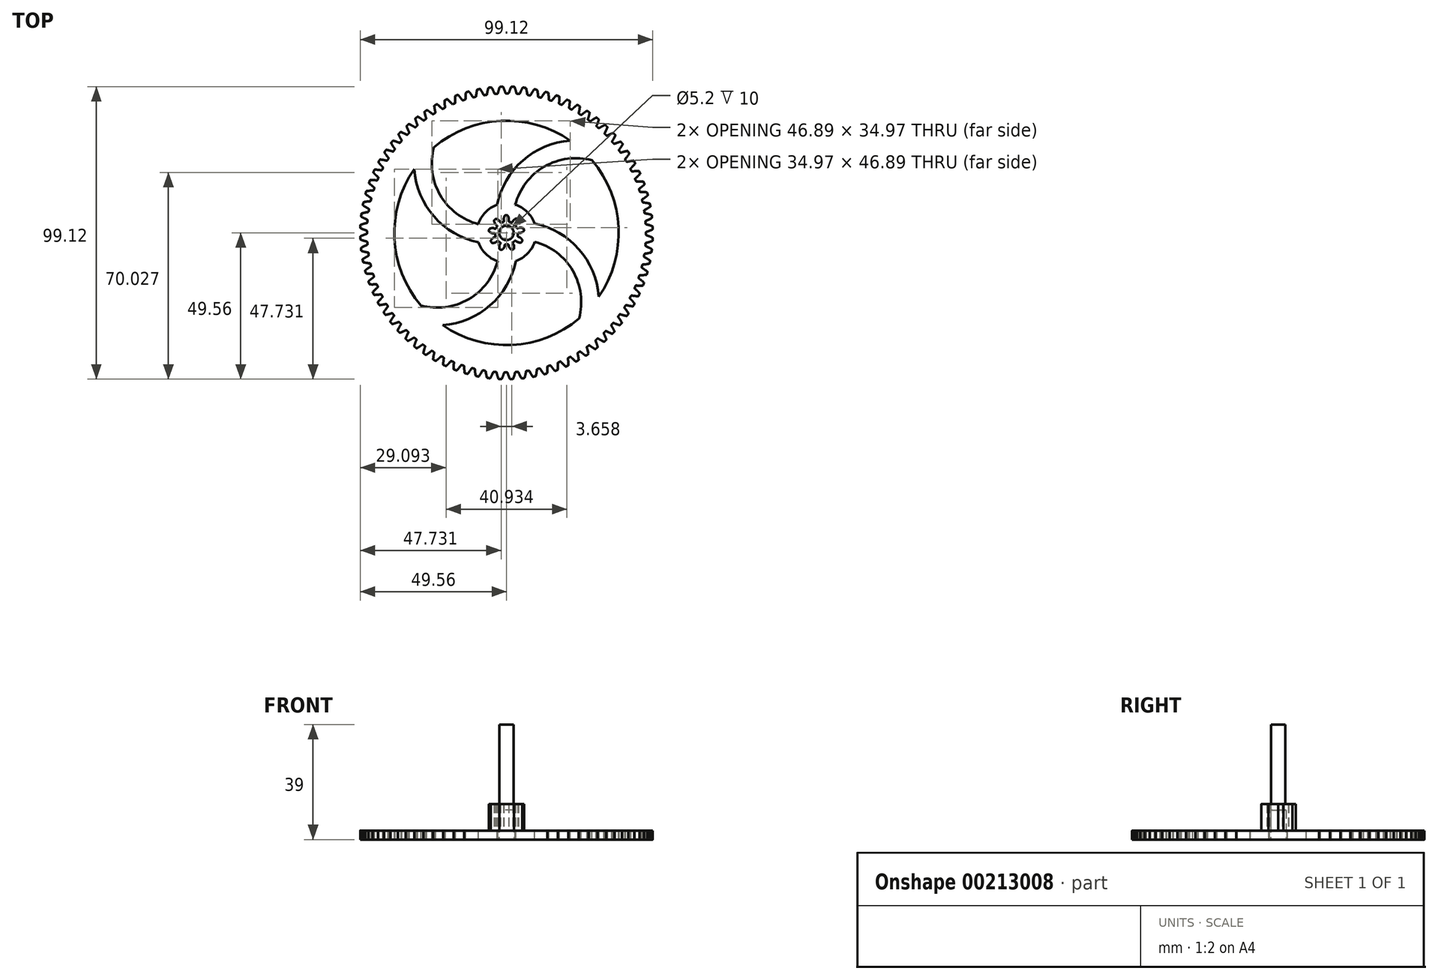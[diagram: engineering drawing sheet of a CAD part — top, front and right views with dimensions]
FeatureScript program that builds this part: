
annotation { "Feature Type Name" : "Feature", "Feature Type Description" : "" }
export const myFeature = defineFeature(function(context is Context, id is Id, definition is map)
    precondition{}
    {
        {
            var Q0;
            Q0=qCreatedBy(makeId("Top.planeOp"),FACE);
            var sketch = newSketch(context, id + "F0", { "sketchPlane" : qUnion([Q0])});
            skCircle(sketch, "E0", {"center": v(0, 0) * mm, "radius": 45.56 * mm, "construction": true});
            skLineSegment(sketch, "E1", {"start": v(0, 0) * mm, "end": v(45.56, 0) * mm, "construction": true});
            skLineSegment(sketch, "E2", {"start": v(45.56, 0) * mm, "end": v(45.56, 0) * mm});
            skLineSegment(sketch, "E3", {"start": v(0, 0) * mm, "end": v(45.52, 1.99) * mm, "construction": true});
            skLineSegment(sketch, "E4", {"start": v(45.52, 1.99) * mm, "end": v(45.6, 0) * mm, "construction": true});
            skLineSegment(sketch, "E5", {"start": v(0, 0) * mm, "end": v(45.39, 3.97) * mm, "construction": true});
            skLineSegment(sketch, "E6", {"start": v(45.39, 3.97) * mm, "end": v(45.73, 0.01) * mm, "construction": true});
            skLineSegment(sketch, "E7", {"start": v(0, 0) * mm, "end": v(45.17, 5.95) * mm, "construction": true});
            skLineSegment(sketch, "E8", {"start": v(45.17, 5.95) * mm, "end": v(45.95, 0.03) * mm, "construction": true});
            skLineSegment(sketch, "E9", {"start": v(0, 0) * mm, "end": v(44.87, 7.91) * mm, "construction": true});
            skLineSegment(sketch, "E10", {"start": v(44.87, 7.91) * mm, "end": v(46.25, 0.08) * mm, "construction": true});
            skLineSegment(sketch, "E11", {"start": v(0, 0) * mm, "end": v(44.48, 9.86) * mm, "construction": true});
            skLineSegment(sketch, "E12", {"start": v(44.48, 9.86) * mm, "end": v(46.63, 0.16) * mm, "construction": true});
            skLineSegment(sketch, "E13", {"start": v(0, 0) * mm, "end": v(44, 11.8) * mm, "construction": true});
            skLineSegment(sketch, "E14", {"start": v(44, 11.8) * mm, "end": v(47.1, 0.27) * mm, "construction": true});
            skLineSegment(sketch, "E15", {"start": v(0, 0) * mm, "end": v(43.45, 13.7) * mm, "construction": true});
            skLineSegment(sketch, "E16", {"start": v(43.45, 13.7) * mm, "end": v(47.64, 0.43) * mm, "construction": true});
            skLineSegment(sketch, "E17", {"start": v(0, 0) * mm, "end": v(42.81, 15.58) * mm, "construction": true});
            skLineSegment(sketch, "E18", {"start": v(42.81, 15.58) * mm, "end": v(48.25, 0.64) * mm, "construction": true});
            skLineSegment(sketch, "E19", {"start": v(0, 0) * mm, "end": v(42.1, 17.44) * mm, "construction": true});
            skLineSegment(sketch, "E20", {"start": v(42.1, 17.44) * mm, "end": v(48.94, 0.9) * mm, "construction": true});
            skLineSegment(sketch, "E21", {"start": v(0, 0) * mm, "end": v(41.3, 19.25) * mm, "construction": true});
            skLineSegment(sketch, "E22", {"start": v(41.3, 19.25) * mm, "end": v(49.7, 1.24) * mm, "construction": true});
            skPoint(sketch, "E23", {"position": v(45.56, 0) * mm});
            skLineSegment(sketch, "E24", {"start": v(0, 0) * mm, "end": v(55.62, 1.92) * mm, "construction": true});
            skFitSpline(sketch, "E25", {"points": [v(45.45, 3.14) * mm, v(45.5, 3.15) * mm, v(45.63, 3.15) * mm, v(45.84, 3.14) * mm, v(46.14, 3.11) * mm, v(46.53, 3.06) * mm, v(47, 2.98) * mm, v(47.55, 2.86) * mm, v(48.18, 2.7) * mm, v(48.89, 2.47) * mm, v(49.66, 2.2) * mm], "startDerivative": vector(1.04, 0.05) * mm, "endDerivative": vector(4.91, -1.82) * mm});
            skFitSpline(sketch, "E26", {"points": [v(45.56, 0) * mm, v(45.6, 0) * mm, v(45.73, 0.01) * mm, v(45.95, 0.03) * mm, v(46.25, 0.08) * mm, v(46.63, 0.16) * mm, v(47.1, 0.27) * mm, v(47.64, 0.43) * mm, v(48.25, 0.64) * mm, v(48.94, 0.9) * mm, v(49.7, 1.24) * mm], "startDerivative": vector(1.04, 0.02) * mm, "endDerivative": vector(4.78, 2.16) * mm});
            skArc(sketch, "E27", {"start": v(49.52, 2.25) * mm, "mid": v(-49.55, -1.71) * mm, "end": v(49.56, 1.18) * mm, "construction": true});
            skArc(sketch, "E28", {"start": v(49.56, 1.18) * mm, "mid": v(49.55, 1.71) * mm, "end": v(49.52, 2.25) * mm});
            skArc(sketch, "E29", {"start": v(47.18, 2.94) * mm, "mid": v(-47.24, -1.63) * mm, "end": v(47.27, 0.32) * mm});
            skArc(sketch, "E30", {"start": v(47.27, 0.32) * mm, "mid": v(47.24, 1.63) * mm, "end": v(47.18, 2.94) * mm, "construction": true});
            skSolve(sketch);
        }
        {
            var Q0;
            Q0=qCreatedBy(makeId("Front.planeOp"),FACE);
            var sketch = newSketch(context, id + "F1", { "sketchPlane" : qUnion([Q0])});
            skLineSegment(sketch, "E31", {"start": v(0, 0) * mm, "end": v(0, 19.36) * mm});
            skSolve(sketch);
        }
        {
            var Q0;
            {var subQ0=sQuery(id+"F0.wireOp",EDGE,"E28");Q0=makeQuery(id+"F0.imprint","IMPRINT",FACE,{"disambiguationData":[TD([[makeQuery(id+"F0.imprint","IMPRINT",EDGE,{"derivedFrom":subQ0}),1.0]])]});}
            extrude(context, id + "F2", {"entities" : qUnion([Q0]), "depth" : 3 * mm});
        }
        {
            var Q0;
            Q0=makeQuery(id+"F2.opExtrude","SWEPT_EDGE",EDGE,{"disambiguationData":[OSD([sQuery(id+"F0.wireOp",EDGE,"E25"),sQuery(id+"F0.wireOp",EDGE,"cd1f8e22-2cf9-43e8-a03b-3c7e5e83a7e11")])]});
            var Q1;
            Q1=makeQuery(id+"F2.opExtrude","SWEPT_EDGE",EDGE,{"disambiguationData":[OSD([sQuery(id+"F0.wireOp",EDGE,"E25"),sQuery(id+"F0.wireOp",EDGE,"6e4f36b8-18ed-47d9-b409-67013e73f9462")])]});
            var Q2;
            Q2=makeQuery(id+"F2.opExtrude","SWEPT_EDGE",EDGE,{"disambiguationData":[OSD([sQuery(id+"F0.wireOp",EDGE,"E26"),sQuery(id+"F0.wireOp",EDGE,"6e4f36b8-18ed-47d9-b409-67013e73f9462")])]});
            var Q3;
            Q3=makeQuery(id+"F2.opExtrude","SWEPT_EDGE",EDGE,{"disambiguationData":[OSD([sQuery(id+"F0.wireOp",EDGE,"E26"),sQuery(id+"F0.wireOp",EDGE,"cd1f8e22-2cf9-43e8-a03b-3c7e5e83a7e11")])]});
            fillet(context, id + "F3", {"entities" : qUnion([Q0, Q1, Q2, Q3]), "radius" : 0.3 * mm, "tangentPropagation" : true, "allowEdgeOverflow" : false});
        }
        {
            var Q0;
            Q0=makeQuery(id+"F2.opExtrude","SWEPT_BODY",BODY,{"disambiguationData":[OSD([sQuery(id+"F0.wireOp",EDGE,"E25"),sQuery(id+"F0.wireOp",EDGE,"E26"),sQuery(id+"F0.wireOp",EDGE,"cd1f8e22-2cf9-43e8-a03b-3c7e5e83a7e11"),sQuery(id+"F0.wireOp",EDGE,"6e4f36b8-18ed-47d9-b409-67013e73f9462")])]});
            var Q1;
            Q1=sQuery(id+"F1.wireOp",EDGE,"E31");
            circularPattern(context, id + "F4", {"operationType" : NewBodyOperationType.ADD, "entities" : qUnion([Q0]), "axis" : qUnion([Q1]), "angle" : 360 * degree, "instanceCount" : 80, "equalSpace" : true});
        }
        {
            var Q0;
            {var subQ0=makeQuery(id+"F2.opExtrude","CAP_FACE",FACE,{"disambiguationData":[OSD([sQuery(id+"F0.wireOp",EDGE,"E25"),sQuery(id+"F0.wireOp",EDGE,"E26"),sQuery(id+"F0.wireOp",EDGE,"cd1f8e22-2cf9-43e8-a03b-3c7e5e83a7e11"),sQuery(id+"F0.wireOp",EDGE,"6e4f36b8-18ed-47d9-b409-67013e73f9462")])],"isStart":false});Q0=makeQuery(id+"F4.boolean.opBoolean","MERGE",FACE,{"derivedFrom":[subQ0,makeQuery(id+"F4.opPattern","COPY",FACE,{"derivedFrom":subQ0,"instanceName":"1"}),makeQuery(id+"F4.opPattern","COPY",FACE,{"derivedFrom":subQ0,"instanceName":"2"}),makeQuery(id+"F4.opPattern","COPY",FACE,{"derivedFrom":subQ0,"instanceName":"3"}),makeQuery(id+"F4.opPattern","COPY",FACE,{"derivedFrom":subQ0,"instanceName":"4"}),makeQuery(id+"F4.opPattern","COPY",FACE,{"derivedFrom":subQ0,"instanceName":"5"}),makeQuery(id+"F4.opPattern","COPY",FACE,{"derivedFrom":subQ0,"instanceName":"6"}),makeQuery(id+"F4.opPattern","COPY",FACE,{"derivedFrom":subQ0,"instanceName":"7"}),makeQuery(id+"F4.opPattern","COPY",FACE,{"derivedFrom":subQ0,"instanceName":"8"}),makeQuery(id+"F4.opPattern","COPY",FACE,{"derivedFrom":subQ0,"instanceName":"9"}),makeQuery(id+"F4.opPattern","COPY",FACE,{"derivedFrom":subQ0,"instanceName":"10"}),makeQuery(id+"F4.opPattern","COPY",FACE,{"derivedFrom":subQ0,"instanceName":"11"}),makeQuery(id+"F4.opPattern","COPY",FACE,{"derivedFrom":subQ0,"instanceName":"12"}),makeQuery(id+"F4.opPattern","COPY",FACE,{"derivedFrom":subQ0,"instanceName":"13"}),makeQuery(id+"F4.opPattern","COPY",FACE,{"derivedFrom":subQ0,"instanceName":"14"}),makeQuery(id+"F4.opPattern","COPY",FACE,{"derivedFrom":subQ0,"instanceName":"15"}),makeQuery(id+"F4.opPattern","COPY",FACE,{"derivedFrom":subQ0,"instanceName":"16"}),makeQuery(id+"F4.opPattern","COPY",FACE,{"derivedFrom":subQ0,"instanceName":"17"}),makeQuery(id+"F4.opPattern","COPY",FACE,{"derivedFrom":subQ0,"instanceName":"18"}),makeQuery(id+"F4.opPattern","COPY",FACE,{"derivedFrom":subQ0,"instanceName":"19"}),makeQuery(id+"F4.opPattern","COPY",FACE,{"derivedFrom":subQ0,"instanceName":"20"}),makeQuery(id+"F4.opPattern","COPY",FACE,{"derivedFrom":subQ0,"instanceName":"21"}),makeQuery(id+"F4.opPattern","COPY",FACE,{"derivedFrom":subQ0,"instanceName":"22"}),makeQuery(id+"F4.opPattern","COPY",FACE,{"derivedFrom":subQ0,"instanceName":"23"}),makeQuery(id+"F4.opPattern","COPY",FACE,{"derivedFrom":subQ0,"instanceName":"24"}),makeQuery(id+"F4.opPattern","COPY",FACE,{"derivedFrom":subQ0,"instanceName":"25"}),makeQuery(id+"F4.opPattern","COPY",FACE,{"derivedFrom":subQ0,"instanceName":"26"}),makeQuery(id+"F4.opPattern","COPY",FACE,{"derivedFrom":subQ0,"instanceName":"27"}),makeQuery(id+"F4.opPattern","COPY",FACE,{"derivedFrom":subQ0,"instanceName":"28"}),makeQuery(id+"F4.opPattern","COPY",FACE,{"derivedFrom":subQ0,"instanceName":"29"}),makeQuery(id+"F4.opPattern","COPY",FACE,{"derivedFrom":subQ0,"instanceName":"30"}),makeQuery(id+"F4.opPattern","COPY",FACE,{"derivedFrom":subQ0,"instanceName":"31"}),makeQuery(id+"F4.opPattern","COPY",FACE,{"derivedFrom":subQ0,"instanceName":"32"}),makeQuery(id+"F4.opPattern","COPY",FACE,{"derivedFrom":subQ0,"instanceName":"33"}),makeQuery(id+"F4.opPattern","COPY",FACE,{"derivedFrom":subQ0,"instanceName":"34"}),makeQuery(id+"F4.opPattern","COPY",FACE,{"derivedFrom":subQ0,"instanceName":"35"}),makeQuery(id+"F4.opPattern","COPY",FACE,{"derivedFrom":subQ0,"instanceName":"36"}),makeQuery(id+"F4.opPattern","COPY",FACE,{"derivedFrom":subQ0,"instanceName":"37"}),makeQuery(id+"F4.opPattern","COPY",FACE,{"derivedFrom":subQ0,"instanceName":"38"}),makeQuery(id+"F4.opPattern","COPY",FACE,{"derivedFrom":subQ0,"instanceName":"39"}),makeQuery(id+"F4.opPattern","COPY",FACE,{"derivedFrom":subQ0,"instanceName":"40"}),makeQuery(id+"F4.opPattern","COPY",FACE,{"derivedFrom":subQ0,"instanceName":"41"}),makeQuery(id+"F4.opPattern","COPY",FACE,{"derivedFrom":subQ0,"instanceName":"42"}),makeQuery(id+"F4.opPattern","COPY",FACE,{"derivedFrom":subQ0,"instanceName":"43"}),makeQuery(id+"F4.opPattern","COPY",FACE,{"derivedFrom":subQ0,"instanceName":"44"}),makeQuery(id+"F4.opPattern","COPY",FACE,{"derivedFrom":subQ0,"instanceName":"45"}),makeQuery(id+"F4.opPattern","COPY",FACE,{"derivedFrom":subQ0,"instanceName":"46"}),makeQuery(id+"F4.opPattern","COPY",FACE,{"derivedFrom":subQ0,"instanceName":"47"}),makeQuery(id+"F4.opPattern","COPY",FACE,{"derivedFrom":subQ0,"instanceName":"48"}),makeQuery(id+"F4.opPattern","COPY",FACE,{"derivedFrom":subQ0,"instanceName":"49"}),makeQuery(id+"F4.opPattern","COPY",FACE,{"derivedFrom":subQ0,"instanceName":"50"}),makeQuery(id+"F4.opPattern","COPY",FACE,{"derivedFrom":subQ0,"instanceName":"51"}),makeQuery(id+"F4.opPattern","COPY",FACE,{"derivedFrom":subQ0,"instanceName":"52"}),makeQuery(id+"F4.opPattern","COPY",FACE,{"derivedFrom":subQ0,"instanceName":"53"}),makeQuery(id+"F4.opPattern","COPY",FACE,{"derivedFrom":subQ0,"instanceName":"54"}),makeQuery(id+"F4.opPattern","COPY",FACE,{"derivedFrom":subQ0,"instanceName":"55"}),makeQuery(id+"F4.opPattern","COPY",FACE,{"derivedFrom":subQ0,"instanceName":"56"}),makeQuery(id+"F4.opPattern","COPY",FACE,{"derivedFrom":subQ0,"instanceName":"57"}),makeQuery(id+"F4.opPattern","COPY",FACE,{"derivedFrom":subQ0,"instanceName":"58"}),makeQuery(id+"F4.opPattern","COPY",FACE,{"derivedFrom":subQ0,"instanceName":"59"}),makeQuery(id+"F4.opPattern","COPY",FACE,{"derivedFrom":subQ0,"instanceName":"60"}),makeQuery(id+"F4.opPattern","COPY",FACE,{"derivedFrom":subQ0,"instanceName":"61"}),makeQuery(id+"F4.opPattern","COPY",FACE,{"derivedFrom":subQ0,"instanceName":"62"}),makeQuery(id+"F4.opPattern","COPY",FACE,{"derivedFrom":subQ0,"instanceName":"63"}),makeQuery(id+"F4.opPattern","COPY",FACE,{"derivedFrom":subQ0,"instanceName":"64"}),makeQuery(id+"F4.opPattern","COPY",FACE,{"derivedFrom":subQ0,"instanceName":"65"}),makeQuery(id+"F4.opPattern","COPY",FACE,{"derivedFrom":subQ0,"instanceName":"66"}),makeQuery(id+"F4.opPattern","COPY",FACE,{"derivedFrom":subQ0,"instanceName":"67"}),makeQuery(id+"F4.opPattern","COPY",FACE,{"derivedFrom":subQ0,"instanceName":"68"}),makeQuery(id+"F4.opPattern","COPY",FACE,{"derivedFrom":subQ0,"instanceName":"69"}),makeQuery(id+"F4.opPattern","COPY",FACE,{"derivedFrom":subQ0,"instanceName":"70"}),makeQuery(id+"F4.opPattern","COPY",FACE,{"derivedFrom":subQ0,"instanceName":"71"}),makeQuery(id+"F4.opPattern","COPY",FACE,{"derivedFrom":subQ0,"instanceName":"72"}),makeQuery(id+"F4.opPattern","COPY",FACE,{"derivedFrom":subQ0,"instanceName":"73"}),makeQuery(id+"F4.opPattern","COPY",FACE,{"derivedFrom":subQ0,"instanceName":"74"}),makeQuery(id+"F4.opPattern","COPY",FACE,{"derivedFrom":subQ0,"instanceName":"75"}),makeQuery(id+"F4.opPattern","COPY",FACE,{"derivedFrom":subQ0,"instanceName":"76"}),makeQuery(id+"F4.opPattern","COPY",FACE,{"derivedFrom":subQ0,"instanceName":"77"}),makeQuery(id+"F4.opPattern","COPY",FACE,{"derivedFrom":subQ0,"instanceName":"78"}),makeQuery(id+"F4.opPattern","COPY",FACE,{"derivedFrom":subQ0,"instanceName":"79"})]});}
            var sketch = newSketch(context, id + "F5", { "sketchPlane" : qUnion([Q0])});
            skCircle(sketch, "E32", {"center": v(0, 0) * mm, "radius": 4.7 * mm, "construction": true});
            skLineSegment(sketch, "E33", {"start": v(0, 0) * mm, "end": v(4.68, 0.38) * mm, "construction": true});
            skLineSegment(sketch, "E34", {"start": v(4.68, 0.38) * mm, "end": v(4.71, 0) * mm, "construction": true});
            skLineSegment(sketch, "E35", {"start": v(0, 0) * mm, "end": v(4.64, 0.75) * mm, "construction": true});
            skLineSegment(sketch, "E36", {"start": v(4.64, 0.75) * mm, "end": v(4.76, 0) * mm, "construction": true});
            skLineSegment(sketch, "E37", {"start": v(0, 0) * mm, "end": v(4.56, 1.12) * mm, "construction": true});
            skLineSegment(sketch, "E38", {"start": v(4.56, 1.12) * mm, "end": v(4.83, 0.02) * mm, "construction": true});
            skLineSegment(sketch, "E39", {"start": v(0, 0) * mm, "end": v(4.46, 1.48) * mm, "construction": true});
            skLineSegment(sketch, "E40", {"start": v(4.46, 1.48) * mm, "end": v(4.93, 0.05) * mm, "construction": true});
            skLineSegment(sketch, "E41", {"start": v(0, 0) * mm, "end": v(4.32, 1.84) * mm, "construction": true});
            skLineSegment(sketch, "E42", {"start": v(4.32, 1.84) * mm, "end": v(5.06, 0.1) * mm, "construction": true});
            skLineSegment(sketch, "E43", {"start": v(0, 0) * mm, "end": v(4.16, 2.18) * mm, "construction": true});
            skLineSegment(sketch, "E44", {"start": v(4.16, 2.18) * mm, "end": v(5.21, 0.17) * mm, "construction": true});
            skLineSegment(sketch, "E45", {"start": v(0, 0) * mm, "end": v(3.98, 2.5) * mm, "construction": true});
            skLineSegment(sketch, "E46", {"start": v(3.98, 2.5) * mm, "end": v(5.38, 0.27) * mm, "construction": true});
            skLineSegment(sketch, "E47", {"start": v(0, 0) * mm, "end": v(3.76, 2.81) * mm, "construction": true});
            skLineSegment(sketch, "E48", {"start": v(3.76, 2.81) * mm, "end": v(5.57, 0.4) * mm, "construction": true});
            skLineSegment(sketch, "E49", {"start": v(0, 0) * mm, "end": v(3.52, 3.1) * mm, "construction": true});
            skLineSegment(sketch, "E50", {"start": v(3.52, 3.1) * mm, "end": v(5.77, 0.56) * mm, "construction": true});
            skLineSegment(sketch, "E51", {"start": v(0, 0) * mm, "end": v(3.26, 3.38) * mm, "construction": true});
            skLineSegment(sketch, "E52", {"start": v(3.26, 3.38) * mm, "end": v(5.98, 0.76) * mm, "construction": true});
            skPoint(sketch, "E53", {"position": v(4.7, 0) * mm});
            skCircle(sketch, "E54", {"center": v(0, 0) * mm, "radius": 3.89 * mm});
            skLineSegment(sketch, "E55", {"start": v(3.89, 0) * mm, "end": v(4.7, 0) * mm});
            skFitSpline(sketch, "E56", {"points": [v(4.7, 0) * mm, v(4.71, 0) * mm, v(4.76, 0) * mm, v(4.83, 0.02) * mm, v(4.93, 0.05) * mm, v(5.06, 0.1) * mm, v(5.21, 0.17) * mm, v(5.38, 0.27) * mm, v(5.57, 0.4) * mm, v(5.77, 0.56) * mm, v(5.98, 0.76) * mm], "startDerivative": vector(0.58, 0) * mm, "endDerivative": vector(1.32, 1.28) * mm});
            skPoint(sketch, "E57", {"position": v(5.95, 0.74) * mm});
            skFitSpline(sketch, "E58", {"points": [v(4.7, 0) * mm, v(4.71, 0) * mm, v(4.76, 0) * mm, v(4.83, 0.02) * mm, v(4.93, 0.05) * mm, v(5.06, 0.1) * mm, v(5.21, 0.17) * mm, v(5.38, 0.27) * mm, v(5.57, 0.4) * mm, v(5.77, 0.56) * mm, v(5.98, 0.76) * mm], "startDerivative": vector(0.58, 0) * mm, "endDerivative": vector(1.32, 1.28) * mm, "construction": true});
            skLineSegment(sketch, "E59", {"start": v(0, 0) * mm, "end": v(7.88, 1.51) * mm, "construction": true});
            skLineSegment(sketch, "E60.MirrorCS", {"start": v(3.61, 1.44) * mm, "end": v(4.37, 1.74) * mm});
            skFitSpline(sketch, "E61.MirrorCS", {"points": [v(4.37, 1.74) * mm, v(4.38, 1.74) * mm, v(4.42, 1.75) * mm, v(4.5, 1.77) * mm, v(4.6, 1.78) * mm, v(4.74, 1.78) * mm, v(4.9, 1.77) * mm, v(5.1, 1.74) * mm, v(5.32, 1.7) * mm, v(5.57, 1.61) * mm, v(5.83, 1.5) * mm], "startDerivative": vector(0.54, 0.22) * mm, "endDerivative": vector(1.7, -0.7) * mm});
            skArc(sketch, "E62", {"start": v(5.8, 1.52) * mm, "mid": v(-5.9, -1.13) * mm, "end": v(5.95, 0.74) * mm, "construction": true});
            skArc(sketch, "E63", {"start": v(5.95, 0.74) * mm, "mid": v(5.9, 1.13) * mm, "end": v(5.8, 1.52) * mm});
            skSolve(sketch);
        }
        {
            var Q0;
            {var subQ1=sQuery(id+"F5.wireOp",EDGE,"E55");Q0=makeQuery(id+"F5.imprint","IMPRINT",FACE,{"disambiguationData":[TD([[makeQuery(id+"F5.imprint","IMPRINT",EDGE,{"derivedFrom":subQ1}),1.0]])]});}
            var Q1;
            {var subQ0=sQuery(id+"F5.wireOp",EDGE,"E54");var subQ1=makeQuery(id+"F5.imprint","INTERSECT",VERTEX,{"derivedFrom":[subQ0,sQuery(id+"F5.wireOp",EDGE,"E55")]});Q1=makeQuery(id+"F5.imprint","IMPRINT",FACE,{"disambiguationData":[TD([[makeQuery(id+"F5.imprint","IMPRINT",EDGE,{"disambiguationData":[TD([[subQ1,-1.0]])],"derivedFrom":subQ0}),1.0]])]});}
            extrude(context, id + "F6", {"entities" : qUnion([Q0, Q1]), "depth" : 9 * mm});
        }
        {
            var Q0;
            Q0=makeQuery(id+"F6.opExtrude","SWEPT_EDGE",EDGE,{"disambiguationData":[OSD([sQuery(id+"F5.wireOp",EDGE,"E54"),sQuery(id+"F5.wireOp",EDGE,"E55")])]});
            var Q1;
            Q1=makeQuery(id+"F6.opExtrude","SWEPT_EDGE",EDGE,{"disambiguationData":[OSD([sQuery(id+"F5.wireOp",EDGE,"E56"),sQuery(id+"F5.wireOp",EDGE,"E63")])]});
            var Q2;
            Q2=makeQuery(id+"F6.opExtrude","SWEPT_EDGE",EDGE,{"disambiguationData":[OSD([sQuery(id+"F5.wireOp",EDGE,"E61.MirrorCS"),sQuery(id+"F5.wireOp",EDGE,"E63")])]});
            var Q3;
            Q3=makeQuery(id+"F6.opExtrude","SWEPT_EDGE",EDGE,{"disambiguationData":[OSD([sQuery(id+"F5.wireOp",EDGE,"E54"),sQuery(id+"F5.wireOp",EDGE,"E60.MirrorCS")])]});
            fillet(context, id + "F7", {"entities" : qUnion([Q0, Q1, Q2, Q3]), "radius" : 0.3 * mm, "tangentPropagation" : true, "allowEdgeOverflow" : false});
        }
        {
            var Q0;
            Q0=makeQuery(id+"F6.opExtrude","SWEPT_BODY",BODY,{"disambiguationData":[OSD([sQuery(id+"F5.wireOp",EDGE,"E54"),sQuery(id+"F5.wireOp",EDGE,"E55"),sQuery(id+"F5.wireOp",EDGE,"E56"),sQuery(id+"F5.wireOp",EDGE,"E60.MirrorCS"),sQuery(id+"F5.wireOp",EDGE,"E61.MirrorCS"),sQuery(id+"F5.wireOp",EDGE,"E63")])]});
            var Q1;
            Q1=sQuery(id+"F1.wireOp",EDGE,"E31");
            circularPattern(context, id + "F8", {"operationType" : NewBodyOperationType.ADD, "entities" : qUnion([Q0]), "axis" : qUnion([Q1]), "angle" : 360 * degree, "instanceCount" : 9, "equalSpace" : true});
        }
        {
            var Q0;
            {var subQ0=makeQuery(id+"F6.opExtrude","CAP_FACE",FACE,{"disambiguationData":[OSD([sQuery(id+"F5.wireOp",EDGE,"E54"),sQuery(id+"F5.wireOp",EDGE,"E55"),sQuery(id+"F5.wireOp",EDGE,"E56"),sQuery(id+"F5.wireOp",EDGE,"E60.MirrorCS"),sQuery(id+"F5.wireOp",EDGE,"E61.MirrorCS"),sQuery(id+"F5.wireOp",EDGE,"E63")])],"isStart":false});Q0=makeQuery(id+"F8.boolean.opBoolean","MERGE",FACE,{"derivedFrom":[subQ0,makeQuery(id+"F8.opPattern","COPY",FACE,{"derivedFrom":subQ0,"instanceName":"1"}),makeQuery(id+"F8.opPattern","COPY",FACE,{"derivedFrom":subQ0,"instanceName":"2"}),makeQuery(id+"F8.opPattern","COPY",FACE,{"derivedFrom":subQ0,"instanceName":"3"}),makeQuery(id+"F8.opPattern","COPY",FACE,{"derivedFrom":subQ0,"instanceName":"4"}),makeQuery(id+"F8.opPattern","COPY",FACE,{"derivedFrom":subQ0,"instanceName":"5"}),makeQuery(id+"F8.opPattern","COPY",FACE,{"derivedFrom":subQ0,"instanceName":"6"}),makeQuery(id+"F8.opPattern","COPY",FACE,{"derivedFrom":subQ0,"instanceName":"7"}),makeQuery(id+"F8.opPattern","COPY",FACE,{"derivedFrom":subQ0,"instanceName":"8"})]});}
            var sketch = newSketch(context, id + "F9", { "sketchPlane" : qUnion([Q0])});
            skCircle(sketch, "E64", {"center": v(0, 0) * mm, "radius": 2.4 * mm});
            skSolve(sketch);
        }
        {
            var Q0;
            Q0=makeQuery(id+"F9.imprint","IMPRINT",FACE,{"disambiguationData":[TD([[makeQuery(id+"F9.imprint","IMPRINT",EDGE,{"derivedFrom":sQuery(id+"F9.wireOp",EDGE,"E64")}),1.0]])]});
            extrude(context, id + "F10", {"entities" : qUnion([Q0]), "operationType" : NewBodyOperationType.ADD, "depth" : 27 * mm});
        }
        {
            var Q0;
            {var subQ0=makeQuery(id+"F2.opExtrude","CAP_FACE",FACE,{"disambiguationData":[OSD([sQuery(id+"F0.wireOp",EDGE,"E25"),sQuery(id+"F0.wireOp",EDGE,"E26"),sQuery(id+"F0.wireOp",EDGE,"cd1f8e22-2cf9-43e8-a03b-3c7e5e83a7e11"),sQuery(id+"F0.wireOp",EDGE,"6e4f36b8-18ed-47d9-b409-67013e73f9462")])],"isStart":false});Q0=makeQuery(id+"F4.boolean.opBoolean","MERGE",FACE,{"derivedFrom":[subQ0,makeQuery(id+"F4.opPattern","COPY",FACE,{"derivedFrom":subQ0,"instanceName":"1"}),makeQuery(id+"F4.opPattern","COPY",FACE,{"derivedFrom":subQ0,"instanceName":"2"}),makeQuery(id+"F4.opPattern","COPY",FACE,{"derivedFrom":subQ0,"instanceName":"3"}),makeQuery(id+"F4.opPattern","COPY",FACE,{"derivedFrom":subQ0,"instanceName":"4"}),makeQuery(id+"F4.opPattern","COPY",FACE,{"derivedFrom":subQ0,"instanceName":"5"}),makeQuery(id+"F4.opPattern","COPY",FACE,{"derivedFrom":subQ0,"instanceName":"6"}),makeQuery(id+"F4.opPattern","COPY",FACE,{"derivedFrom":subQ0,"instanceName":"7"}),makeQuery(id+"F4.opPattern","COPY",FACE,{"derivedFrom":subQ0,"instanceName":"8"}),makeQuery(id+"F4.opPattern","COPY",FACE,{"derivedFrom":subQ0,"instanceName":"9"}),makeQuery(id+"F4.opPattern","COPY",FACE,{"derivedFrom":subQ0,"instanceName":"10"}),makeQuery(id+"F4.opPattern","COPY",FACE,{"derivedFrom":subQ0,"instanceName":"11"}),makeQuery(id+"F4.opPattern","COPY",FACE,{"derivedFrom":subQ0,"instanceName":"12"}),makeQuery(id+"F4.opPattern","COPY",FACE,{"derivedFrom":subQ0,"instanceName":"13"}),makeQuery(id+"F4.opPattern","COPY",FACE,{"derivedFrom":subQ0,"instanceName":"14"}),makeQuery(id+"F4.opPattern","COPY",FACE,{"derivedFrom":subQ0,"instanceName":"15"}),makeQuery(id+"F4.opPattern","COPY",FACE,{"derivedFrom":subQ0,"instanceName":"16"}),makeQuery(id+"F4.opPattern","COPY",FACE,{"derivedFrom":subQ0,"instanceName":"17"}),makeQuery(id+"F4.opPattern","COPY",FACE,{"derivedFrom":subQ0,"instanceName":"18"}),makeQuery(id+"F4.opPattern","COPY",FACE,{"derivedFrom":subQ0,"instanceName":"19"}),makeQuery(id+"F4.opPattern","COPY",FACE,{"derivedFrom":subQ0,"instanceName":"20"}),makeQuery(id+"F4.opPattern","COPY",FACE,{"derivedFrom":subQ0,"instanceName":"21"}),makeQuery(id+"F4.opPattern","COPY",FACE,{"derivedFrom":subQ0,"instanceName":"22"}),makeQuery(id+"F4.opPattern","COPY",FACE,{"derivedFrom":subQ0,"instanceName":"23"}),makeQuery(id+"F4.opPattern","COPY",FACE,{"derivedFrom":subQ0,"instanceName":"24"}),makeQuery(id+"F4.opPattern","COPY",FACE,{"derivedFrom":subQ0,"instanceName":"25"}),makeQuery(id+"F4.opPattern","COPY",FACE,{"derivedFrom":subQ0,"instanceName":"26"}),makeQuery(id+"F4.opPattern","COPY",FACE,{"derivedFrom":subQ0,"instanceName":"27"}),makeQuery(id+"F4.opPattern","COPY",FACE,{"derivedFrom":subQ0,"instanceName":"28"}),makeQuery(id+"F4.opPattern","COPY",FACE,{"derivedFrom":subQ0,"instanceName":"29"}),makeQuery(id+"F4.opPattern","COPY",FACE,{"derivedFrom":subQ0,"instanceName":"30"}),makeQuery(id+"F4.opPattern","COPY",FACE,{"derivedFrom":subQ0,"instanceName":"31"}),makeQuery(id+"F4.opPattern","COPY",FACE,{"derivedFrom":subQ0,"instanceName":"32"}),makeQuery(id+"F4.opPattern","COPY",FACE,{"derivedFrom":subQ0,"instanceName":"33"}),makeQuery(id+"F4.opPattern","COPY",FACE,{"derivedFrom":subQ0,"instanceName":"34"}),makeQuery(id+"F4.opPattern","COPY",FACE,{"derivedFrom":subQ0,"instanceName":"35"}),makeQuery(id+"F4.opPattern","COPY",FACE,{"derivedFrom":subQ0,"instanceName":"36"}),makeQuery(id+"F4.opPattern","COPY",FACE,{"derivedFrom":subQ0,"instanceName":"37"}),makeQuery(id+"F4.opPattern","COPY",FACE,{"derivedFrom":subQ0,"instanceName":"38"}),makeQuery(id+"F4.opPattern","COPY",FACE,{"derivedFrom":subQ0,"instanceName":"39"}),makeQuery(id+"F4.opPattern","COPY",FACE,{"derivedFrom":subQ0,"instanceName":"40"}),makeQuery(id+"F4.opPattern","COPY",FACE,{"derivedFrom":subQ0,"instanceName":"41"}),makeQuery(id+"F4.opPattern","COPY",FACE,{"derivedFrom":subQ0,"instanceName":"42"}),makeQuery(id+"F4.opPattern","COPY",FACE,{"derivedFrom":subQ0,"instanceName":"43"}),makeQuery(id+"F4.opPattern","COPY",FACE,{"derivedFrom":subQ0,"instanceName":"44"}),makeQuery(id+"F4.opPattern","COPY",FACE,{"derivedFrom":subQ0,"instanceName":"45"}),makeQuery(id+"F4.opPattern","COPY",FACE,{"derivedFrom":subQ0,"instanceName":"46"}),makeQuery(id+"F4.opPattern","COPY",FACE,{"derivedFrom":subQ0,"instanceName":"47"}),makeQuery(id+"F4.opPattern","COPY",FACE,{"derivedFrom":subQ0,"instanceName":"48"}),makeQuery(id+"F4.opPattern","COPY",FACE,{"derivedFrom":subQ0,"instanceName":"49"}),makeQuery(id+"F4.opPattern","COPY",FACE,{"derivedFrom":subQ0,"instanceName":"50"}),makeQuery(id+"F4.opPattern","COPY",FACE,{"derivedFrom":subQ0,"instanceName":"51"}),makeQuery(id+"F4.opPattern","COPY",FACE,{"derivedFrom":subQ0,"instanceName":"52"}),makeQuery(id+"F4.opPattern","COPY",FACE,{"derivedFrom":subQ0,"instanceName":"53"}),makeQuery(id+"F4.opPattern","COPY",FACE,{"derivedFrom":subQ0,"instanceName":"54"}),makeQuery(id+"F4.opPattern","COPY",FACE,{"derivedFrom":subQ0,"instanceName":"55"}),makeQuery(id+"F4.opPattern","COPY",FACE,{"derivedFrom":subQ0,"instanceName":"56"}),makeQuery(id+"F4.opPattern","COPY",FACE,{"derivedFrom":subQ0,"instanceName":"57"}),makeQuery(id+"F4.opPattern","COPY",FACE,{"derivedFrom":subQ0,"instanceName":"58"}),makeQuery(id+"F4.opPattern","COPY",FACE,{"derivedFrom":subQ0,"instanceName":"59"}),makeQuery(id+"F4.opPattern","COPY",FACE,{"derivedFrom":subQ0,"instanceName":"60"}),makeQuery(id+"F4.opPattern","COPY",FACE,{"derivedFrom":subQ0,"instanceName":"61"}),makeQuery(id+"F4.opPattern","COPY",FACE,{"derivedFrom":subQ0,"instanceName":"62"}),makeQuery(id+"F4.opPattern","COPY",FACE,{"derivedFrom":subQ0,"instanceName":"63"}),makeQuery(id+"F4.opPattern","COPY",FACE,{"derivedFrom":subQ0,"instanceName":"64"}),makeQuery(id+"F4.opPattern","COPY",FACE,{"derivedFrom":subQ0,"instanceName":"65"}),makeQuery(id+"F4.opPattern","COPY",FACE,{"derivedFrom":subQ0,"instanceName":"66"}),makeQuery(id+"F4.opPattern","COPY",FACE,{"derivedFrom":subQ0,"instanceName":"67"}),makeQuery(id+"F4.opPattern","COPY",FACE,{"derivedFrom":subQ0,"instanceName":"68"}),makeQuery(id+"F4.opPattern","COPY",FACE,{"derivedFrom":subQ0,"instanceName":"69"}),makeQuery(id+"F4.opPattern","COPY",FACE,{"derivedFrom":subQ0,"instanceName":"70"}),makeQuery(id+"F4.opPattern","COPY",FACE,{"derivedFrom":subQ0,"instanceName":"71"}),makeQuery(id+"F4.opPattern","COPY",FACE,{"derivedFrom":subQ0,"instanceName":"72"}),makeQuery(id+"F4.opPattern","COPY",FACE,{"derivedFrom":subQ0,"instanceName":"73"}),makeQuery(id+"F4.opPattern","COPY",FACE,{"derivedFrom":subQ0,"instanceName":"74"}),makeQuery(id+"F4.opPattern","COPY",FACE,{"derivedFrom":subQ0,"instanceName":"75"}),makeQuery(id+"F4.opPattern","COPY",FACE,{"derivedFrom":subQ0,"instanceName":"76"}),makeQuery(id+"F4.opPattern","COPY",FACE,{"derivedFrom":subQ0,"instanceName":"77"}),makeQuery(id+"F4.opPattern","COPY",FACE,{"derivedFrom":subQ0,"instanceName":"78"}),makeQuery(id+"F4.opPattern","COPY",FACE,{"derivedFrom":subQ0,"instanceName":"79"})]});}
            var sketch = newSketch(context, id + "F11", { "sketchPlane" : qUnion([Q0])});
            skCircle(sketch, "E65", {"center": v(0, 0) * mm, "radius": 10 * mm});
            skCircle(sketch, "E66", {"center": v(0, 0) * mm, "radius": 38 * mm});
            skLineSegment(sketch, "E67", {"start": v(0, 0) * mm, "end": v(25.43, 28.24) * mm, "construction": true});
            skCircle(sketch, "E68", {"center": v(23.48, 4.1) * mm, "radius": 24.2 * mm, "construction": true});
            skPoint(sketch, "E68.first.point", {"position": v(0, 10) * mm});
            skPoint(sketch, "E68.third.point", {"position": v(14.17, 26.46) * mm});
            skArc(sketch, "E69", {"start": v(21.62, 31.25) * mm, "mid": v(5.53, 24.56) * mm, "end": v(-3.2, 9.48) * mm});
            skArc(sketch, "E70", {"start": v(28.97, 24.6) * mm, "mid": v(12.85, 22.46) * mm, "end": v(2.98, 9.55) * mm});
            skArc(sketch, "E71.1.0", {"start": v(-31.25, 21.62) * mm, "mid": v(-24.56, 5.53) * mm, "end": v(-9.48, -3.2) * mm});
            skArc(sketch, "E71.1.1", {"start": v(-24.6, 28.97) * mm, "mid": v(-22.46, 12.85) * mm, "end": v(-9.55, 2.98) * mm});
            skArc(sketch, "E71.2.0", {"start": v(-21.62, -31.25) * mm, "mid": v(-5.53, -24.56) * mm, "end": v(3.2, -9.48) * mm});
            skArc(sketch, "E71.2.1", {"start": v(-28.97, -24.6) * mm, "mid": v(-12.85, -22.46) * mm, "end": v(-2.98, -9.55) * mm});
            skArc(sketch, "E71.3.0", {"start": v(31.25, -21.62) * mm, "mid": v(24.56, -5.53) * mm, "end": v(9.48, 3.2) * mm});
            skArc(sketch, "E71.3.1", {"start": v(24.6, -28.97) * mm, "mid": v(22.46, -12.85) * mm, "end": v(9.55, -2.98) * mm});
            skSolve(sketch);
        }
        {
            var Q0;
            {var subQ0=sQuery(id+"F11.wireOp",EDGE,"E69");Q0=makeQuery(id+"F11.imprint","IMPRINT",FACE,{"disambiguationData":[TD([[makeQuery(id+"F11.imprint","IMPRINT",EDGE,{"derivedFrom":subQ0}),-1.0]])]});}
            var Q1;
            {var subQ0=sQuery(id+"F11.wireOp",EDGE,"E71.1.0");Q1=makeQuery(id+"F11.imprint","IMPRINT",FACE,{"disambiguationData":[TD([[makeQuery(id+"F11.imprint","IMPRINT",EDGE,{"derivedFrom":subQ0}),-1.0]])]});}
            var Q2;
            {var subQ0=sQuery(id+"F11.wireOp",EDGE,"E71.2.0");Q2=makeQuery(id+"F11.imprint","IMPRINT",FACE,{"disambiguationData":[TD([[makeQuery(id+"F11.imprint","IMPRINT",EDGE,{"derivedFrom":subQ0}),-1.0]])]});}
            var Q3;
            {var subQ0=sQuery(id+"F11.wireOp",EDGE,"E70");Q3=makeQuery(id+"F11.imprint","IMPRINT",FACE,{"disambiguationData":[TD([[makeQuery(id+"F11.imprint","IMPRINT",EDGE,{"derivedFrom":subQ0}),1.0]])]});}
            extrude(context, id + "F12", {"entities" : qUnion([Q0, Q1, Q2, Q3]), "operationType" : NewBodyOperationType.REMOVE, "endBound" : BoundingType.UP_TO_NEXT, "oppositeDirection" : true, "depth" : 25 * mm});
        }
        {
            var Q0;
            {var subQ0=sQuery(id+"F0.wireOp",EDGE,"E28");Q0=makeQuery(id+"F0.imprint","IMPRINT",FACE,{"disambiguationData":[TD([[makeQuery(id+"F0.imprint","IMPRINT",EDGE,{"derivedFrom":subQ0}),1.0]])]});}
            var sketch = newSketch(context, id + "F13", { "sketchPlane" : qUnion([Q0])});
            skCircle(sketch, "E72", {"center": v(0, 0) * mm, "radius": 2.6 * mm});
            skSolve(sketch);
        }
        {
            var Q0;
            Q0=makeQuery(id+"F13.imprint","IMPRINT",FACE,{"disambiguationData":[TD([[makeQuery(id+"F13.imprint","IMPRINT",EDGE,{"derivedFrom":sQuery(id+"F13.wireOp",EDGE,"E72")}),1.0]])]});
            extrude(context, id + "F14", {"entities" : qUnion([Q0]), "operationType" : NewBodyOperationType.REMOVE, "depth" : 10 * mm});
        }
    });
